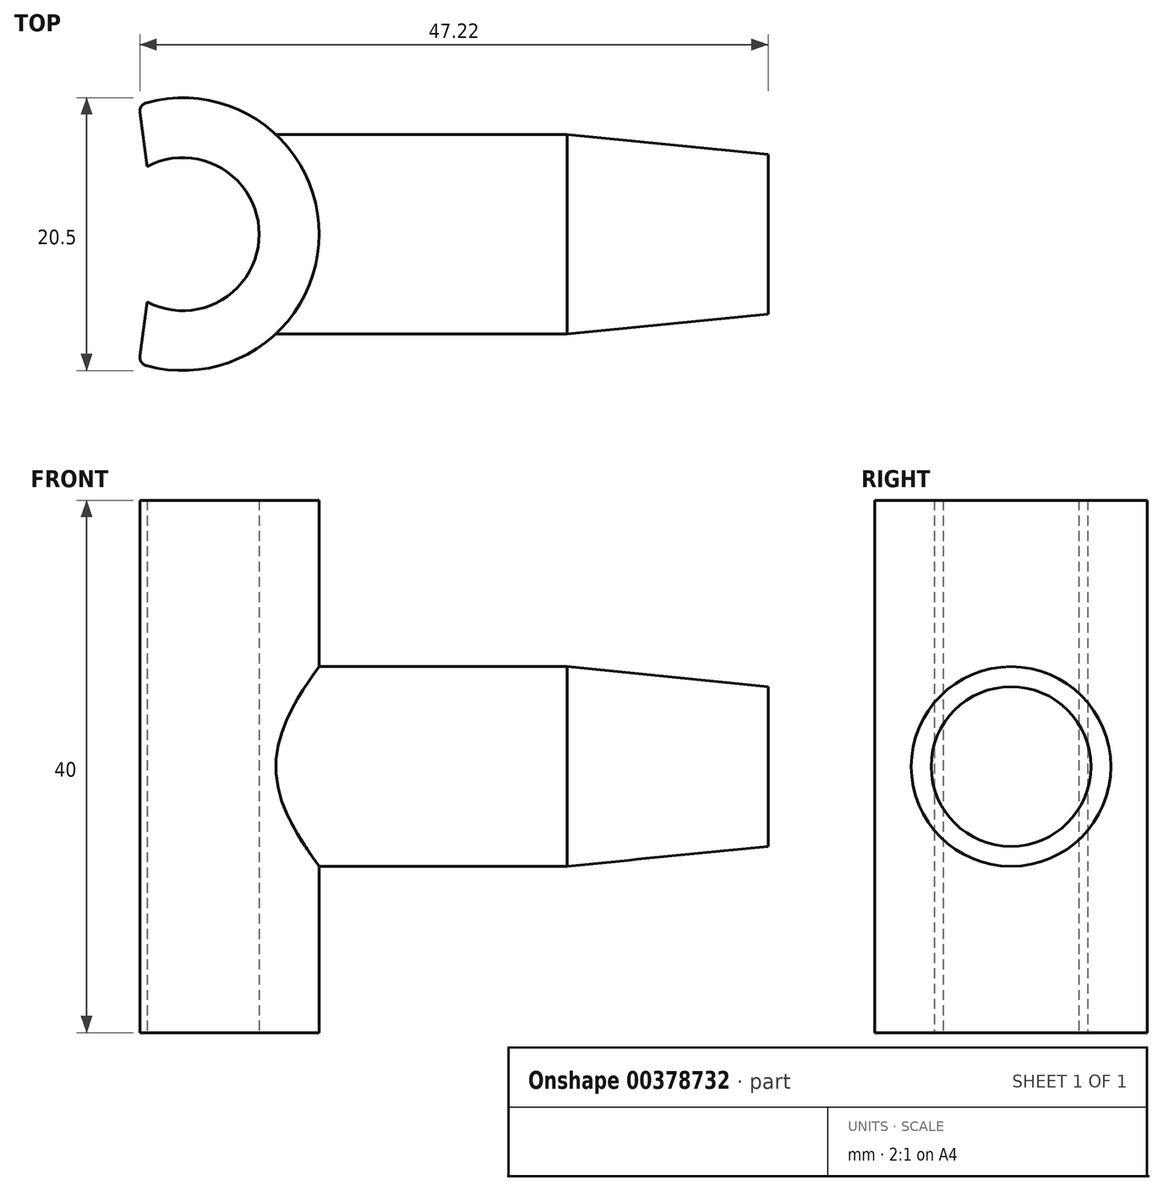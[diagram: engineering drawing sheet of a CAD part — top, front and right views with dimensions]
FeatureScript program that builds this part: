
annotation { "Feature Type Name" : "Feature", "Feature Type Description" : "" }
export const myFeature = defineFeature(function(context is Context, id is Id, definition is map)
    precondition{}
    {
        {
            var Q0;
            Q0=qCreatedBy(makeId("Top.planeOp"),FACE);
            var sketch = newSketch(context, id + "F0", { "sketchPlane" : qUnion([Q0])});
            skArc(sketch, "E0.0", {"start": v(-2.71, -9.88) * mm, "mid": v(10.25, 0) * mm, "end": v(-2.71, 9.88) * mm});
            skLineSegment(sketch, "E1", {"start": v(-2.67, 5.09) * mm, "end": v(-3.21, 9.13) * mm});
            skLineSegment(sketch, "E2", {"start": v(-2.67, -5.09) * mm, "end": v(-3.21, -9.13) * mm});
            skPoint(sketch, "E3.orphan", {"position": v(-3.29, -12.3) * mm});
            skPoint(sketch, "E4.visualSharp", {"position": v(-3.29, -9.7) * mm});
            skArc(sketch, "E4.filletArc", {"start": v(-3.21, -9.13) * mm, "mid": v(-3.1, -9.6) * mm, "end": v(-2.71, -9.88) * mm});
            skPoint(sketch, "E5.visualSharp", {"position": v(-3.29, 9.7) * mm});
            skArc(sketch, "E5.filletArc", {"start": v(-2.71, 9.88) * mm, "mid": v(-3.1, 9.6) * mm, "end": v(-3.21, 9.13) * mm});
            skArc(sketch, "E6.0", {"start": v(-2.67, -5.09) * mm, "mid": v(5.75, 0) * mm, "end": v(-2.67, 5.09) * mm});
            skSolve(sketch);
        }
        {
            var Q0;
            Q0=qCreatedBy(makeId("Right.planeOp"),FACE);
            cPlane(context, id + "F1", {"entities" : qUnion([Q0]), "cplaneType" : CPlaneType.OFFSET, "offset" : 4 * mm, "width" : 150 * mm, "height" : 150 * mm});
        }
        {
            var Q0;
            Q0=qCreatedBy(id+"F1.planeOp",FACE);
            var sketch = newSketch(context, id + "F2", { "sketchPlane" : qUnion([Q0])});
            skCircle(sketch, "E7", {"center": v(0, 0) * mm, "radius": 7.5 * mm});
            skSolve(sketch);
        }
        {
            var Q0;
            Q0 = qSketchRegion(id + "F2", true);
            extrude(context, id + "F3", {"entities" : qUnion([Q0]), "depth" : 40 * mm});
        }
        {
            var Q0;
            Q0=makeQuery(id+"F3.opExtrude","CAP_EDGE",EDGE,{"disambiguationData":[OSD([sQuery(id+"F2.wireOp",EDGE,"E7")])],"isStart":false});
            chamfer(context, id + "F4", {"entities" : qUnion([Q0]), "chamferType" : ChamferType.TWO_OFFSETS, "width1" : 1.5 * mm, "oppositeDirection" : false, "width2" : 15.1 * mm, "tangentPropagation" : true});
        }
        {
            var Q0;
            Q0=makeQuery(id+"F2.imprint","IMPRINT",FACE,{"disambiguationData":[TD([[makeQuery(id+"F2.imprint","IMPRINT",EDGE,{"derivedFrom":sQuery(id+"F2.wireOp",EDGE,"E7")}),1.0]])]});
            extrude(context, id + "F5", {"entities" : qUnion([Q0]), "operationType" : NewBodyOperationType.REMOVE, "depth" : 2.5 * mm});
        }
        {
            var Q0;
            Q0 = qSketchRegion(id + "F0", true);
            extrude(context, id + "F6", {"entities" : qUnion([Q0]), "operationType" : NewBodyOperationType.ADD, "endBound" : BoundingType.SYMMETRIC, "depth" : 40 * mm});
        }
    });
